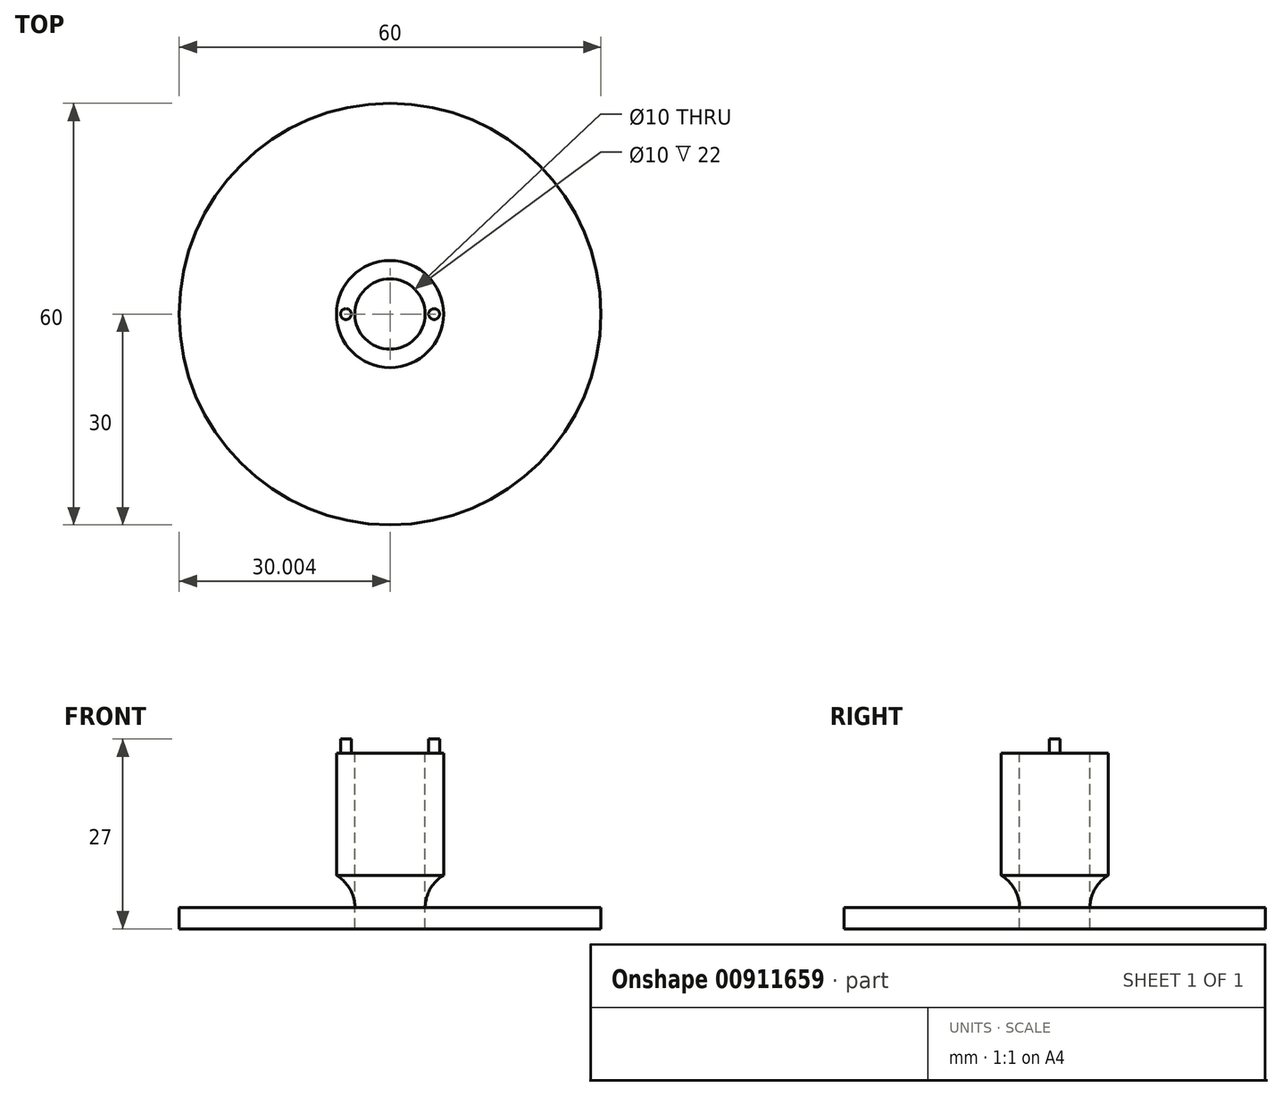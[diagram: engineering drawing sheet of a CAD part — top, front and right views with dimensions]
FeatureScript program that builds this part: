
annotation { "Feature Type Name" : "Feature", "Feature Type Description" : "" }
export const myFeature = defineFeature(function(context is Context, id is Id, definition is map)
    precondition{}
    {
        {
            var Q0;
            Q0=qCreatedBy(makeId("Front.planeOp"),FACE);
            var sketch = newSketch(context, id + "F0", { "sketchPlane" : qUnion([Q0])});
            skLineSegment(sketch, "E0.bottom", {"start": v(-1.13, 0) * mm, "end": v(23.87, 0) * mm});
            skLineSegment(sketch, "E0.top", {"start": v(-1.13, 3) * mm, "end": v(23.87, 3) * mm});
            skLineSegment(sketch, "E0.left", {"start": v(-1.13, 0) * mm, "end": v(-1.13, 3) * mm});
            skLineSegment(sketch, "E0.right", {"start": v(23.87, 0) * mm, "end": v(23.87, 3) * mm});
            skLineSegment(sketch, "E1.bottom", {"start": v(-1.13, 0) * mm, "end": v(-6.13, 0) * mm});
            skLineSegment(sketch, "E1.top", {"start": v(-1.13, 25) * mm, "end": v(-6.13, 25) * mm});
            skLineSegment(sketch, "E1.left", {"start": v(-1.13, 0) * mm, "end": v(-1.13, 25) * mm});
            skLineSegment(sketch, "E1.right", {"start": v(-6.13, 0) * mm, "end": v(-6.13, 25) * mm});
            skArc(sketch, "E2", {"start": v(1.5, 7.6) * mm, "mid": v(-0.43, 5.64) * mm, "end": v(-1.13, 3) * mm});
            skLineSegment(sketch, "E3", {"start": v(1.5, 7.6) * mm, "end": v(1.5, 25) * mm});
            skLineSegment(sketch, "E4", {"start": v(1.5, 25) * mm, "end": v(-1.13, 25) * mm});
            skSolve(sketch);
        }
        {
            var Q0;
            {var subQ0=sQuery(id+"F0.wireOp",EDGE,"E0.bottom");Q0=makeQuery(id+"F0.imprint","IMPRINT",FACE,{"disambiguationData":[TD([[makeQuery(id+"F0.imprint","IMPRINT",EDGE,{"derivedFrom":subQ0}),1.0]])]});}
            var Q1;
            {var subQ0=sQuery(id+"F0.wireOp",EDGE,"E2");Q1=makeQuery(id+"F0.imprint","IMPRINT",FACE,{"disambiguationData":[TD([[makeQuery(id+"F0.imprint","IMPRINT",EDGE,{"derivedFrom":subQ0}),-1.0]])]});}
            var Q2;
            {var subQ3=sQuery(id+"F0.wireOp",EDGE,"E1.bottom");Q2=makeQuery(id+"F0.imprint","IMPRINT",FACE,{"disambiguationData":[TD([[makeQuery(id+"F0.imprint","IMPRINT",EDGE,{"derivedFrom":subQ3}),-1.0]])]});}
            var Q3;
            Q3=sQuery(id+"F0.wireOp",EDGE,"E1.right");
            revolve(context, id + "F1", {"surfaceOperationType" : NewSurfaceOperationType.NEW, "entities" : qUnion([Q0, Q1, Q2]), "axis" : qUnion([Q3]), "revolveType" : RevolveType.FULL});
        }
        {
            var Q0;
            Q0=makeQuery(id+"F1.opRevolve","SWEPT_FACE",FACE,{"disambiguationData":[OSD([sQuery(id+"F0.wireOp",EDGE,"E1.top"),sQuery(id+"F0.wireOp",EDGE,"E4")])]});
            var sketch = newSketch(context, id + "F2", { "sketchPlane" : qUnion([Q0])});
            skCircle(sketch, "E5", {"center": v(-6.13, 0) * mm, "radius": 5 * mm});
            skSolve(sketch);
        }
        {
            var Q0;
            Q0 = qSketchRegion(id + "F2", true);
            extrude(context, id + "F3", {"entities" : qUnion([Q0]), "operationType" : NewBodyOperationType.REMOVE, "oppositeDirection" : true, "depth" : 34.4 * mm, "offsetDistance" : 25 * mm});
        }
        {
            var Q0;
            Q0=makeQuery(id+"F1.opRevolve","SWEPT_FACE",FACE,{"disambiguationData":[OSD([sQuery(id+"F0.wireOp",EDGE,"E1.top"),sQuery(id+"F0.wireOp",EDGE,"E4")])]});
            var sketch = newSketch(context, id + "F4", { "sketchPlane" : qUnion([Q0])});
            skCircle(sketch, "E6", {"center": v(-12.4, 0) * mm, "radius": 0.78 * mm});
            skPoint(sketch, "E7", {"position": v(-11.13, 0) * mm});
            skPoint(sketch, "E8", {"position": v(-13.74, 0) * mm});
            skCircle(sketch, "E9", {"center": v(0.15, 0) * mm, "radius": 0.78 * mm});
            skSolve(sketch);
        }
        {
            var Q0;
            Q0 = qSketchRegion(id + "F4", true);
            extrude(context, id + "F5", {"entities" : qUnion([Q0]), "operationType" : NewBodyOperationType.ADD, "depth" : 2 * mm, "offsetDistance" : 25 * mm});
        }
    });
